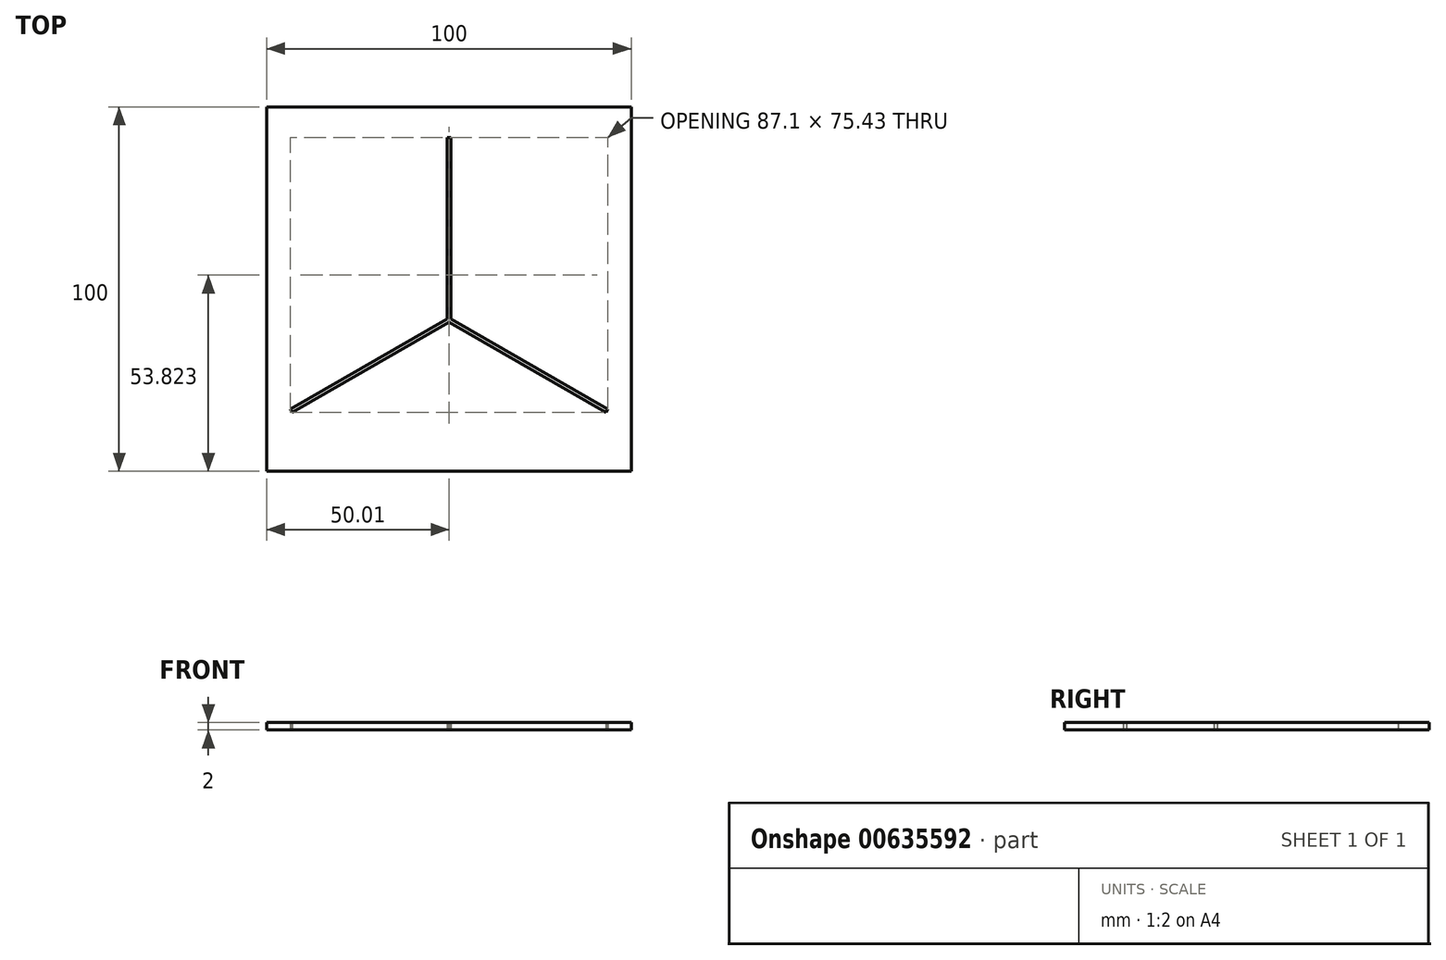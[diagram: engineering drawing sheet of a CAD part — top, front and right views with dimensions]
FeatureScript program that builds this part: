
annotation { "Feature Type Name" : "Feature", "Feature Type Description" : "" }
export const myFeature = defineFeature(function(context is Context, id is Id, definition is map)
    precondition{}
    {
        {
            var Q0;
            Q0=qCreatedBy(makeId("Top.planeOp"),FACE);
            var sketch = newSketch(context, id + "F0", { "sketchPlane" : qUnion([Q0])});
            skLineSegment(sketch, "E0.bottom", {"start": v(50, 58.46) * mm, "end": v(-50, 58.46) * mm});
            skLineSegment(sketch, "E0.top", {"start": v(50, -41.54) * mm, "end": v(-50, -41.54) * mm});
            skLineSegment(sketch, "E0.left", {"start": v(50, 58.46) * mm, "end": v(50, -41.54) * mm});
            skLineSegment(sketch, "E0.right", {"start": v(-50, 58.46) * mm, "end": v(-50, -41.54) * mm});
            skLineSegment(sketch, "E1", {"start": v(0, 50) * mm, "end": v(-0.5, 50) * mm});
            skLineSegment(sketch, "E2", {"start": v(-0.5, 50) * mm, "end": v(0, 50) * mm});
            skLineSegment(sketch, "E3", {"start": v(0.5, 50) * mm, "end": v(0.5, 0) * mm});
            skLineSegment(sketch, "E4", {"start": v(0.5, 50) * mm, "end": v(0, 50) * mm});
            skLineSegment(sketch, "E5", {"start": v(-0.5, 50) * mm, "end": v(-0.5, 0) * mm});
            skLineSegment(sketch, "E6.1.0", {"start": v(-43.05, -25.43) * mm, "end": v(0.25, -0.43) * mm});
            skLineSegment(sketch, "E6.1.1", {"start": v(-43.55, -24.57) * mm, "end": v(-0.25, 0.43) * mm});
            skLineSegment(sketch, "E6.1.2", {"start": v(-43.55, -24.57) * mm, "end": v(-43.3, -25) * mm});
            skLineSegment(sketch, "E6.1.3", {"start": v(-43.05, -25.43) * mm, "end": v(-43.3, -25) * mm});
            skLineSegment(sketch, "E6.1.4", {"start": v(-43.3, -25) * mm, "end": v(-43.05, -25.43) * mm});
            skLineSegment(sketch, "E6.2.0", {"start": v(43.55, -24.57) * mm, "end": v(0.25, 0.43) * mm});
            skLineSegment(sketch, "E6.2.1", {"start": v(43.05, -25.43) * mm, "end": v(-0.25, -0.43) * mm});
            skLineSegment(sketch, "E6.2.2", {"start": v(43.05, -25.43) * mm, "end": v(43.3, -25) * mm});
            skLineSegment(sketch, "E6.2.3", {"start": v(43.55, -24.57) * mm, "end": v(43.3, -25) * mm});
            skLineSegment(sketch, "E6.2.4", {"start": v(43.3, -25) * mm, "end": v(43.55, -24.57) * mm});
            skPoint(sketch, "E6.center", {"position": v(0, 0) * mm});
            skSolve(sketch);
        }
        {
            var Q0;
            Q0 = qSketchRegion(id + "F0", true);
            extrude(context, id + "F1", {"entities" : qUnion([Q0]), "depth" : 2 * mm, "offsetDistance" : 25 * mm});
        }
    });
